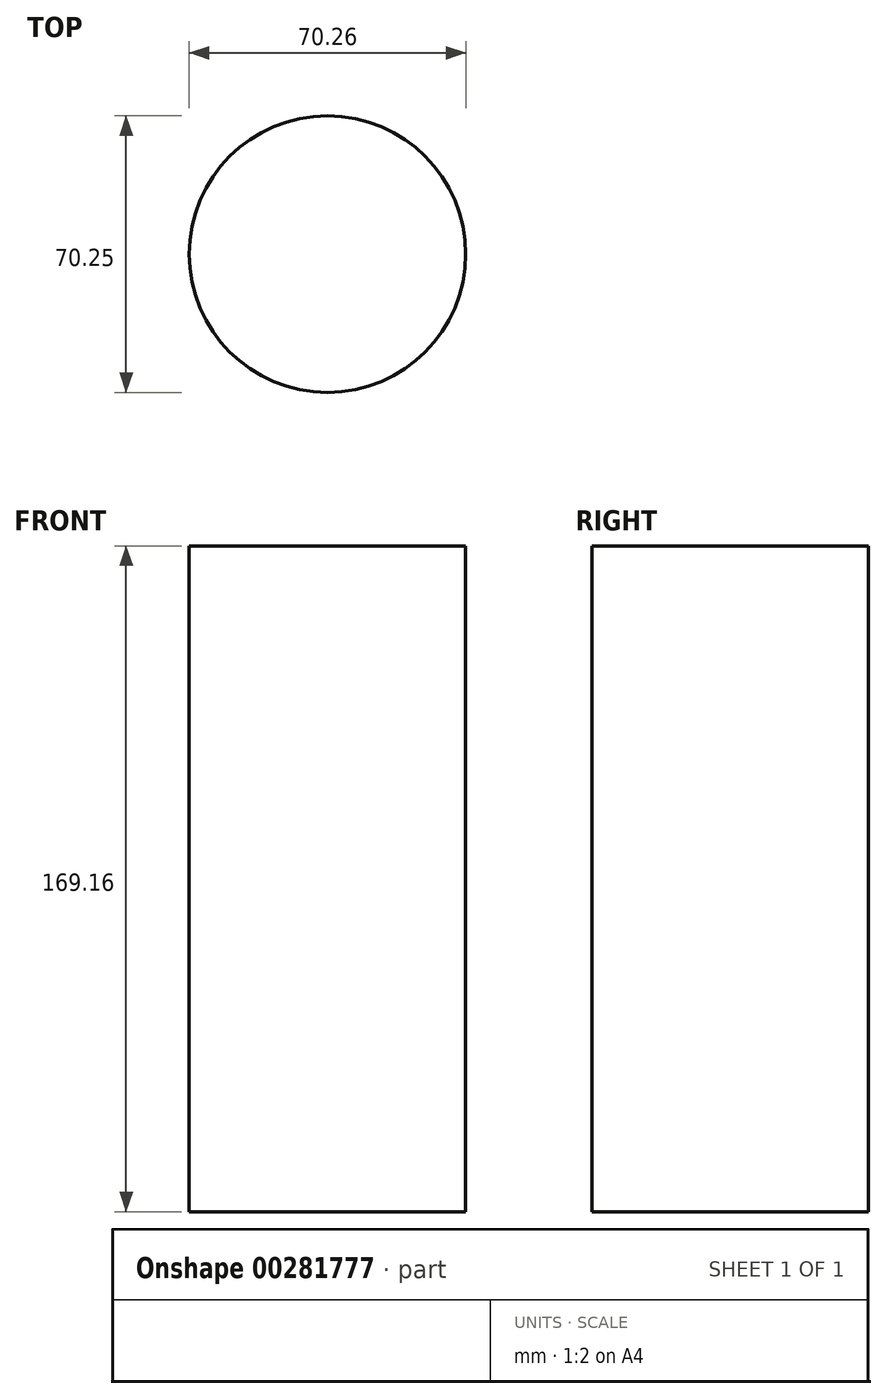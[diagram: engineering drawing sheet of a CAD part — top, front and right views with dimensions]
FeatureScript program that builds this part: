
annotation { "Feature Type Name" : "Feature", "Feature Type Description" : "" }
export const myFeature = defineFeature(function(context is Context, id is Id, definition is map)
    precondition{}
    {
        {
            var Q0;
            Q0=qCreatedBy(makeId("Top.planeOp"),FACE);
            var sketch = newSketch(context, id + "F0", { "sketchPlane" : qUnion([Q0])});
            skCircle(sketch, "E0", {"center": v(-50.9, 38.93) * mm, "radius": 35.13 * mm});
            skSolve(sketch);
        }
        {
            var Q0;
            Q0=makeQuery(id+"F0.imprint","IMPRINT",FACE,{"disambiguationData":[TD([[makeQuery(id+"F0.imprint","IMPRINT",EDGE,{"derivedFrom":sQuery(id+"F0.wireOp",EDGE,"E0")}),1.0]])]});
            extrude(context, id + "F1", {"entities" : qUnion([Q0]), "depth" : 169.16 * mm});
        }
    });
